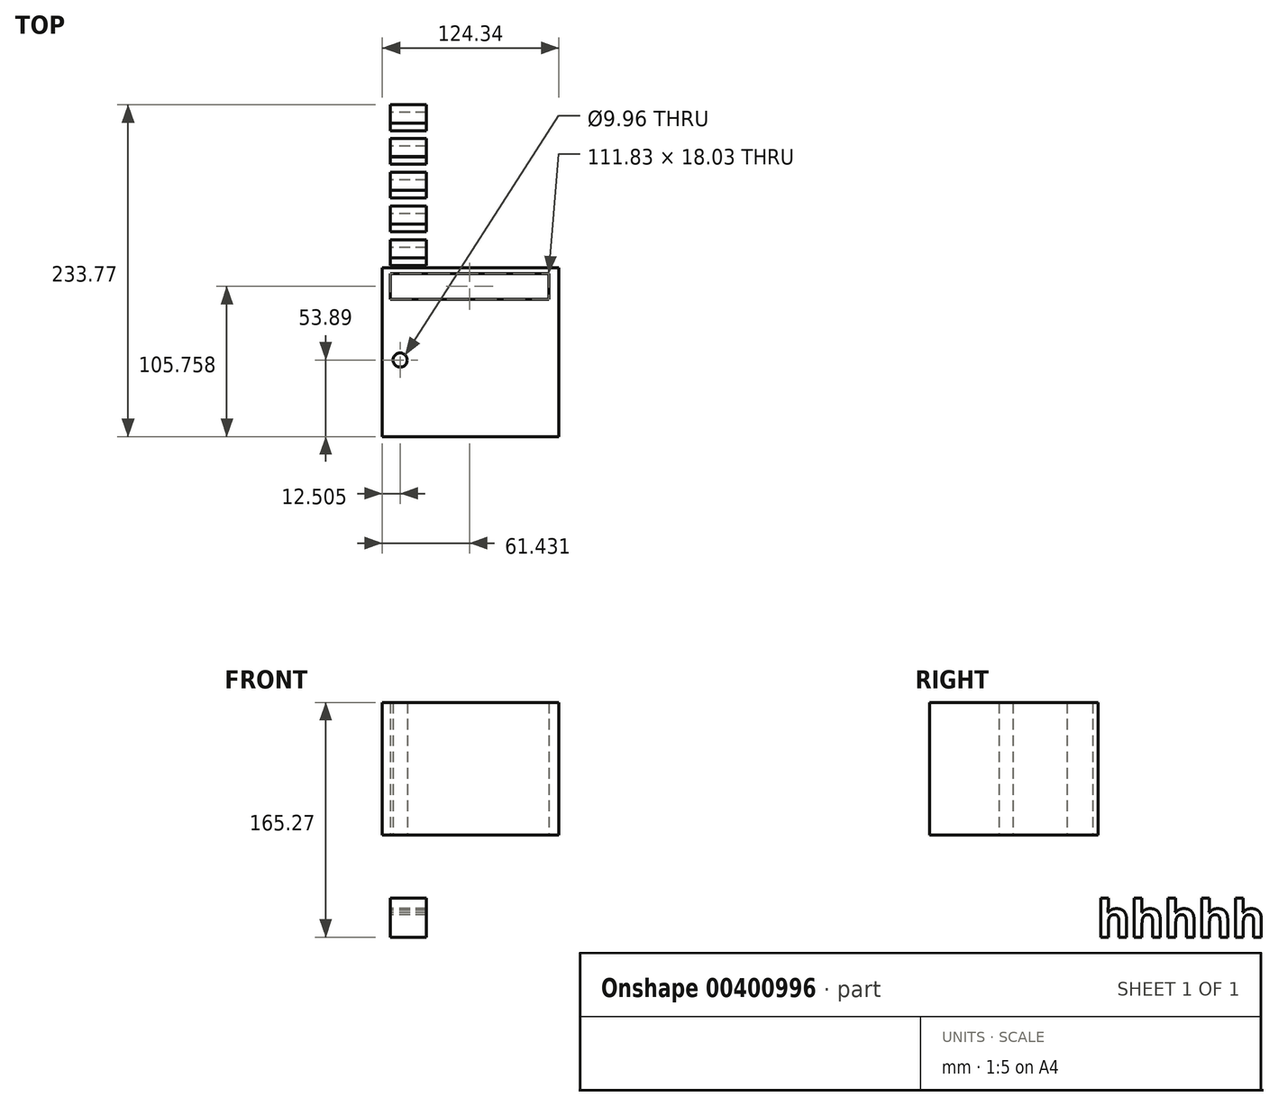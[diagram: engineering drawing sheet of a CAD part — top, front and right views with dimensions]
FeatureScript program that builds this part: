
annotation { "Feature Type Name" : "Feature", "Feature Type Description" : "" }
export const myFeature = defineFeature(function(context is Context, id is Id, definition is map)
    precondition{}
    {
        {
            var Q0;
            Q0=qCreatedBy(makeId("Top.planeOp"),FACE);
            var sketch = newSketch(context, id + "F0", { "sketchPlane" : qUnion([Q0])});
            skLineSegment(sketch, "E0.bottom", {"start": v(-68.42, 64.93) * mm, "end": v(55.92, 64.93) * mm});
            skLineSegment(sketch, "E0.top", {"start": v(-68.42, -53.9) * mm, "end": v(55.92, -53.9) * mm});
            skLineSegment(sketch, "E0.left", {"start": v(-68.42, 64.93) * mm, "end": v(-68.42, -53.9) * mm});
            skLineSegment(sketch, "E0.right", {"start": v(55.92, 64.93) * mm, "end": v(55.92, -53.9) * mm});
            skLineSegment(sketch, "E1.bottom", {"start": v(-62.9, 60.88) * mm, "end": v(48.93, 60.88) * mm});
            skLineSegment(sketch, "E1.top", {"start": v(-62.9, 42.86) * mm, "end": v(48.93, 42.86) * mm});
            skLineSegment(sketch, "E1.left", {"start": v(-62.9, 60.88) * mm, "end": v(-62.9, 42.86) * mm});
            skLineSegment(sketch, "E1.right", {"start": v(48.93, 60.88) * mm, "end": v(48.93, 42.86) * mm});
            skCircle(sketch, "E2", {"center": v(-55.92, 0) * mm, "radius": 4.98 * mm});
            skSolve(sketch);
        }
        {
            var Q0;
            Q0 = qSketchRegion(id + "F0", true);
            extrude(context, id + "F1", {"entities" : qUnion([Q0]), "depth" : 25.4 * mm});
        }
        {
            var Q0;
            Q0=makeQuery(id+"F1.opExtrude","CAP_FACE",FACE,{"disambiguationData":[OSD([sQuery(id+"F0.wireOp",EDGE,"E0.bottom"),sQuery(id+"F0.wireOp",EDGE,"E0.top"),sQuery(id+"F0.wireOp",EDGE,"E0.left"),sQuery(id+"F0.wireOp",EDGE,"E0.right"),sQuery(id+"F0.wireOp",EDGE,"E1.bottom"),sQuery(id+"F0.wireOp",EDGE,"E1.top"),sQuery(id+"F0.wireOp",EDGE,"E1.left"),sQuery(id+"F0.wireOp",EDGE,"E1.right"),sQuery(id+"F0.wireOp",EDGE,"E2")])],"isStart":false});
            var sketch = newSketch(context, id + "F2", { "sketchPlane" : qUnion([Q0])});
            skSolve(sketch);
        }
        {
            var Q0;
            Q0=makeQuery(id+"F2.imprint","IMPRINT",FACE,{"disambiguationData":[TD([[makeQuery(id+"F2.imprint","IMPRINT",EDGE,{"derivedFrom":makeQuery(id+"F1.opExtrude","CAP_EDGE",EDGE,{"disambiguationData":[OSD([sQuery(id+"F0.wireOp",EDGE,"E0.bottom")])],"isStart":false})}),-1.0]])]});
            extrude(context, id + "F3", {"entities" : qUnion([Q0]), "operationType" : NewBodyOperationType.ADD, "depth" : 68.07 * mm});
        }
        {
            var Q0;
            {var subQ0=sQuery(id+"F0.wireOp",EDGE,"E1.left");Q0=makeQuery(id+"F3.boolean.opBoolean","MERGE",FACE,{"derivedFrom":[makeQuery(id+"F1.opExtrude","SWEPT_FACE",FACE,{"disambiguationData":[OSD([subQ0])]}),makeQuery(id+"F3.opExtrude","SWEPT_FACE",FACE,{"disambiguationData":[OSD([subQ0])]})]});}
            var sketch = newSketch(context, id + "F4", { "sketchPlane" : qUnion([Q0])});
            skText(sketch, "E3", { "text": "hhhhh", "fontName": "OpenSans-Bold.ttf"});
            const initialGuessF4  = {"E3": [0.0638, -0.0718, 1, 0, 0.02603]};
            skSetInitialGuess(sketch, initialGuessF4);
            skSolve(sketch);
        }
        {
            var Q0;
            Q0 = qSketchRegion(id + "F4", true);
            extrude(context, id + "F5", {"entities" : qUnion([Q0]), "depth" : 25.4 * mm});
        }
    });
